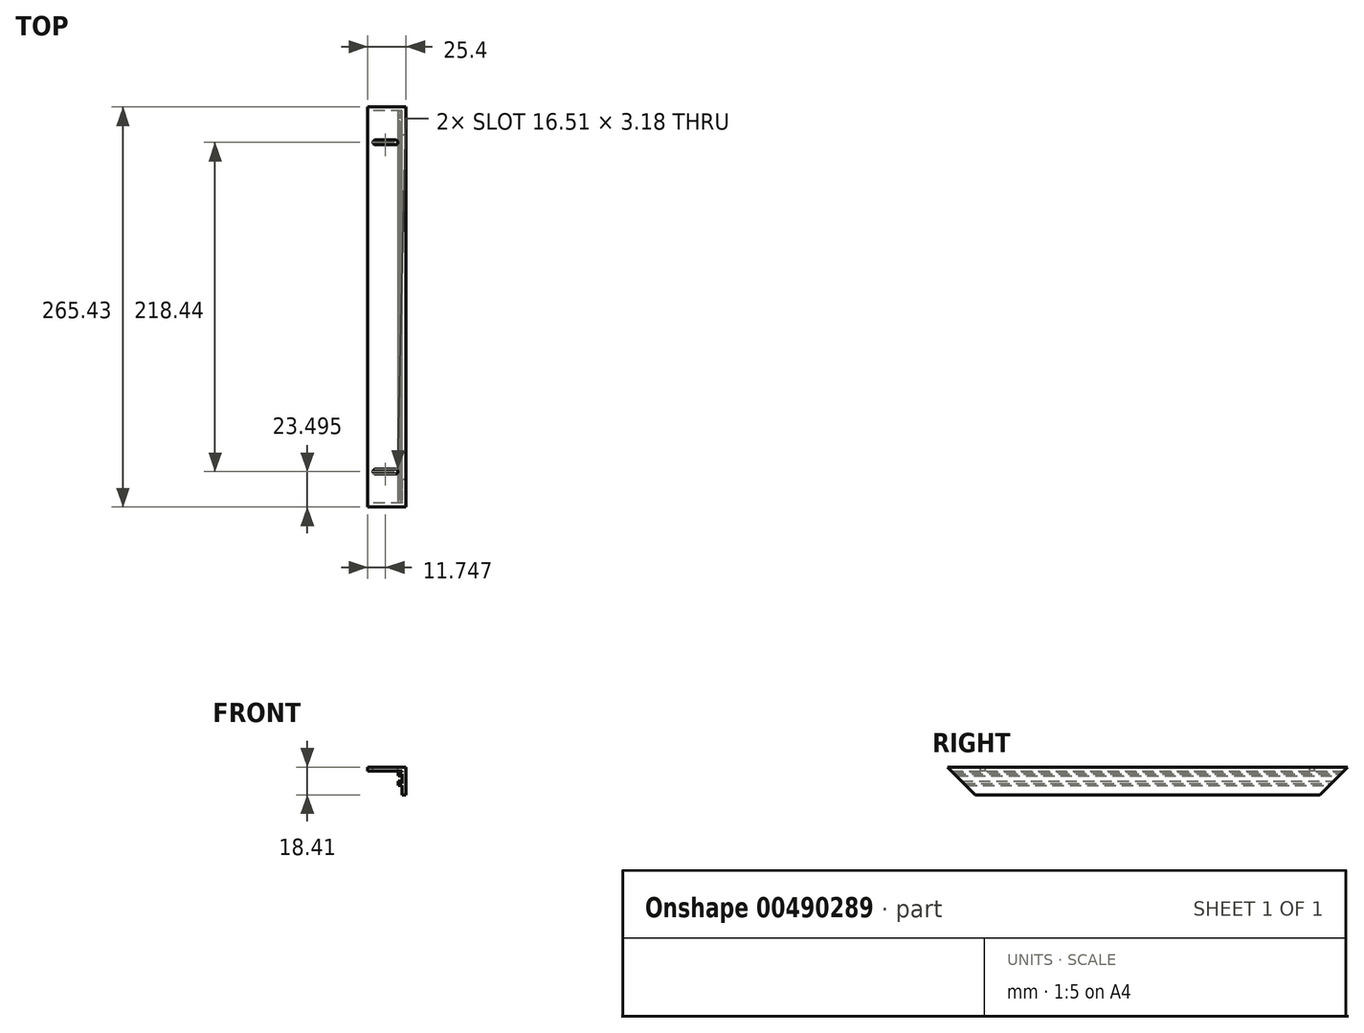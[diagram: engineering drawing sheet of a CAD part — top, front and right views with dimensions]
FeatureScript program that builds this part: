
annotation { "Feature Type Name" : "Feature", "Feature Type Description" : "" }
export const myFeature = defineFeature(function(context is Context, id is Id, definition is map)
    precondition{}
    {
        {
            var Q0;
            Q0=qCreatedBy(makeId("Front.planeOp"),FACE);
            var sketch = newSketch(context, id + "F0", { "sketchPlane" : qUnion([Q0])});
            skLineSegment(sketch, "E0", {"start": v(0, 0) * mm, "end": v(0, 18.41) * mm});
            skLineSegment(sketch, "E1", {"start": v(0, 18.41) * mm, "end": v(-25.4, 18.41) * mm});
            skLineSegment(sketch, "E2", {"start": v(-25.4, 18.41) * mm, "end": v(-25.4, 15.87) * mm});
            skLineSegment(sketch, "E3", {"start": v(-25.4, 15.87) * mm, "end": v(-2.54, 15.88) * mm});
            skLineSegment(sketch, "E4", {"start": v(-2.54, 15.88) * mm, "end": v(-2.54, 15.24) * mm});
            skLineSegment(sketch, "E5", {"start": v(-2.54, 0) * mm, "end": v(0, 0) * mm});
            skLineSegment(sketch, "E6", {"start": v(-2.54, 15.24) * mm, "end": v(-5.08, 15.24) * mm});
            skLineSegment(sketch, "E7", {"start": v(-5.08, 15.24) * mm, "end": v(-5.08, 12.45) * mm});
            skLineSegment(sketch, "E8", {"start": v(-5.08, 6.35) * mm, "end": v(-2.54, 6.35) * mm});
            skLineSegment(sketch, "E9.trimOffspring", {"start": v(-2.54, 6.35) * mm, "end": v(-2.54, 0) * mm});
            skLineSegment(sketch, "E10.bottom", {"start": v(-2.54, 13.97) * mm, "end": v(-3.81, 13.97) * mm});
            skLineSegment(sketch, "E10.top", {"start": v(-2.54, 7.62) * mm, "end": v(-3.8, 7.62) * mm});
            skLineSegment(sketch, "E10.left", {"start": v(-2.54, 13.97) * mm, "end": v(-2.54, 7.62) * mm});
            skLineSegment(sketch, "E10.right", {"start": v(-3.81, 13.97) * mm, "end": v(-3.81, 12.45) * mm});
            skLineSegment(sketch, "E11", {"start": v(-5.08, 12.45) * mm, "end": v(-3.81, 12.45) * mm});
            skLineSegment(sketch, "E12", {"start": v(-5.08, 9.14) * mm, "end": v(-3.81, 9.14) * mm});
            skLineSegment(sketch, "E13.trimOffspring", {"start": v(-5.08, 9.14) * mm, "end": v(-5.08, 6.35) * mm});
            skLineSegment(sketch, "E14.trimOffspring", {"start": v(-3.81, 9.14) * mm, "end": v(-3.81, 7.62) * mm});
            skSolve(sketch);
        }
        {
            var Q0;
            Q0 = qSketchRegion(id + "F0", true);
            extrude(context, id + "F1", {"entities" : qUnion([Q0]), "depth" : 265.43 * mm});
        }
        {
            var Q0;
            Q0=makeQuery(id+"F1.opExtrude","SWEPT_FACE",FACE,{"disambiguationData":[OSD([sQuery(id+"F0.wireOp",EDGE,"E0")])]});
            var sketch = newSketch(context, id + "F2", { "sketchPlane" : qUnion([Q0])});
            skLineSegment(sketch, "E15", {"start": v(-265.43, 18.41) * mm, "end": v(-265.43, 0) * mm});
            skLineSegment(sketch, "E16", {"start": v(-265.43, 0) * mm, "end": v(-247.02, 0) * mm});
            skLineSegment(sketch, "E17", {"start": v(-247.02, 0) * mm, "end": v(-265.43, 18.41) * mm});
            skLineSegment(sketch, "E18", {"start": v(0, 18.41) * mm, "end": v(0, 0) * mm});
            skLineSegment(sketch, "E19", {"start": v(0, 0) * mm, "end": v(-18.41, 0) * mm});
            skLineSegment(sketch, "E20", {"start": v(-18.41, 0) * mm, "end": v(0, 18.41) * mm});
            skSolve(sketch);
        }
        {
            var Q0;
            Q0 = qSketchRegion(id + "F2", true);
            extrude(context, id + "F3", {"entities" : qUnion([Q0]), "operationType" : NewBodyOperationType.REMOVE, "oppositeDirection" : true, "depth" : 25.4 * mm});
        }
        {
            var Q0;
            Q0=makeQuery(id+"F1.opExtrude","SWEPT_FACE",FACE,{"disambiguationData":[OSD([sQuery(id+"F0.wireOp",EDGE,"E1")])]});
            var sketch = newSketch(context, id + "F4", { "sketchPlane" : qUnion([Q0])});
            skLineSegment(sketch, "E21", {"start": v(-25.4, -132.72) * mm, "end": v(0, -132.72) * mm, "construction": true});
            skLineSegment(sketch, "E22", {"start": v(-20.32, -240.35) * mm, "end": v(-6.99, -240.35) * mm});
            skLineSegment(sketch, "E23", {"start": v(-20.32, -243.52) * mm, "end": v(-6.99, -243.52) * mm});
            skArc(sketch, "E24", {"start": v(-20.32, -240.35) * mm, "mid": v(-21.9, -241.94) * mm, "end": v(-20.32, -243.52) * mm});
            skArc(sketch, "E25", {"start": v(-6.99, -243.52) * mm, "mid": v(-5.4, -241.94) * mm, "end": v(-6.99, -240.35) * mm});
            skArc(sketch, "E26.MirrorCS", {"start": v(-20.32, -25.08) * mm, "mid": v(-21.9, -23.5) * mm, "end": v(-20.32, -21.9) * mm});
            skArc(sketch, "E27.MirrorCS", {"start": v(-6.99, -21.9) * mm, "mid": v(-5.4, -23.5) * mm, "end": v(-6.99, -25.08) * mm});
            skLineSegment(sketch, "E28.MirrorCS", {"start": v(-20.32, -25.08) * mm, "end": v(-6.99, -25.08) * mm});
            skLineSegment(sketch, "E29.MirrorCS", {"start": v(-20.32, -21.9) * mm, "end": v(-6.99, -21.9) * mm});
            skSolve(sketch);
        }
        {
            var Q0;
            Q0 = qSketchRegion(id + "F4", true);
            extrude(context, id + "F5", {"entities" : qUnion([Q0]), "operationType" : NewBodyOperationType.REMOVE, "oppositeDirection" : true, "depth" : 2.54 * mm});
        }
    });
